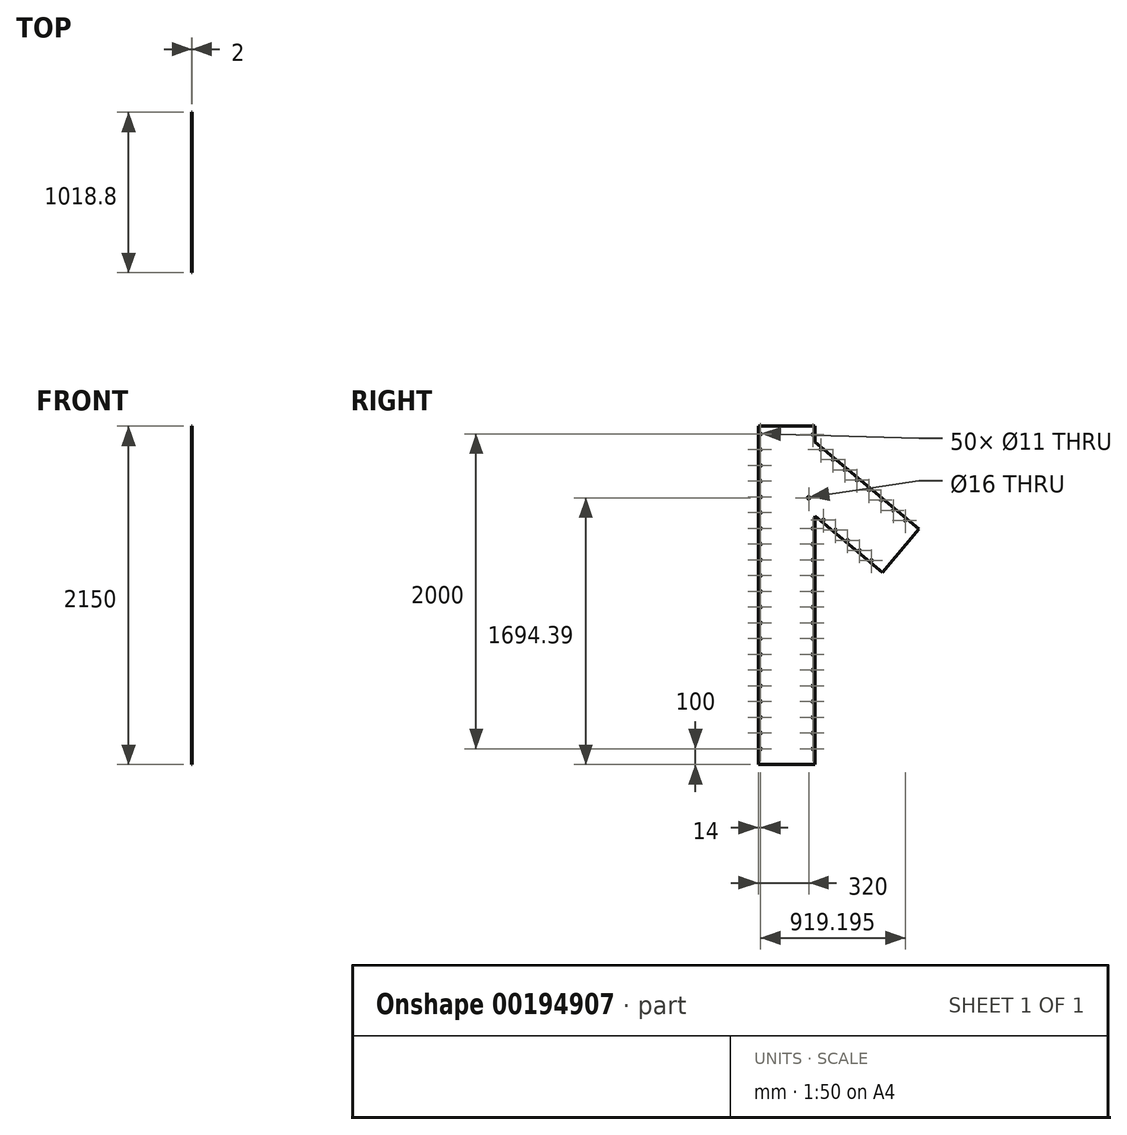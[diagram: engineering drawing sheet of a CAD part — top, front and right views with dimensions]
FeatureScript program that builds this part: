
annotation { "Feature Type Name" : "Feature", "Feature Type Description" : "" }
export const myFeature = defineFeature(function(context is Context, id is Id, definition is map)
    precondition{}
    {
        {
            var Q0;
            Q0=qCreatedBy(makeId("Right.planeOp"),FACE);
            var sketch = newSketch(context, id + "F0", { "sketchPlane" : qUnion([Q0])});
            skLineSegment(sketch, "E0", {"start": v(0, 0) * mm, "end": v(0, 2050) * mm});
            skLineSegment(sketch, "E1", {"start": v(360, 2050) * mm, "end": v(1018.8, 1497.2) * mm});
            skLineSegment(sketch, "E2", {"start": v(1018.8, 1497.2) * mm, "end": v(787.4, 1221.43) * mm});
            skLineSegment(sketch, "E3", {"start": v(360, 1580.05) * mm, "end": v(360, 0) * mm});
            skLineSegment(sketch, "E4", {"start": v(360, 0) * mm, "end": v(0, 0) * mm});
            skLineSegment(sketch, "E5", {"start": v(360, 2050) * mm, "end": v(360, 2150) * mm});
            skLineSegment(sketch, "E6", {"start": v(360, 2150) * mm, "end": v(0, 2150) * mm});
            skLineSegment(sketch, "E7", {"start": v(0, 2150) * mm, "end": v(0, 2050) * mm});
            skLineSegment(sketch, "E8", {"start": v(787.4, 1221.43) * mm, "end": v(360, 1580.05) * mm});
            skSolve(sketch);
        }
        {
            var Q0;
            Q0 = qSketchRegion(id + "F0", true);
            extrude(context, id + "F1", {"entities" : qUnion([Q0]), "depth" : 2 * mm});
        }
        {
            var Q0;
            Q0=makeQuery(id+"F1.opExtrude","CAP_FACE",FACE,{"disambiguationData":[OSD([sQuery(id+"F0.wireOp",EDGE,"E0"),sQuery(id+"F0.wireOp",EDGE,"E1"),sQuery(id+"F0.wireOp",EDGE,"E2"),sQuery(id+"F0.wireOp",EDGE,"E3"),sQuery(id+"F0.wireOp",EDGE,"E4"),sQuery(id+"F0.wireOp",EDGE,"E5"),sQuery(id+"F0.wireOp",EDGE,"E6"),sQuery(id+"F0.wireOp",EDGE,"E7"),sQuery(id+"F0.wireOp",EDGE,"E8")])],"isStart":false});
            var sketch = newSketch(context, id + "F2", { "sketchPlane" : qUnion([Q0])});
            skCircle(sketch, "E9", {"center": v(320, 1694.39) * mm, "radius": 8 * mm});
            skLineSegment(sketch, "E10", {"start": v(806.68, 1244.4) * mm, "end": v(330, 1644.39) * mm, "construction": true});
            skLineSegment(sketch, "E11", {"start": v(330, 1644.39) * mm, "end": v(330, 0) * mm, "construction": true});
            skLineSegment(sketch, "E12", {"start": v(14, 0) * mm, "end": v(14, 2150) * mm, "construction": true});
            skLineSegment(sketch, "E13", {"start": v(346, 2150) * mm, "end": v(346, 2043.47) * mm, "construction": true});
            skLineSegment(sketch, "E14", {"start": v(346, 2043.47) * mm, "end": v(1009.8, 1486.48) * mm, "construction": true});
            skLineSegment(sketch, "E15", {"start": v(796.4, 1232.15) * mm, "end": v(346, 1610.08) * mm, "construction": true});
            skLineSegment(sketch, "E16", {"start": v(346, 1610.08) * mm, "end": v(346, 0) * mm, "construction": true});
            skCircle(sketch, "E17", {"center": v(14, 100) * mm, "radius": 5.5 * mm});
            skCircle(sketch, "E18", {"center": v(346, 100) * mm, "radius": 5.5 * mm});
            skCircle(sketch, "E19", {"center": v(719.79, 1296.43) * mm, "radius": 5.5 * mm});
            skCircle(sketch, "E20", {"center": v(933.2, 1550.76) * mm, "radius": 5.5 * mm});
            skCircle(sketch, "E21", {"center": v(346, 2096.74) * mm, "radius": 5.5 * mm});
            skCircle(sketch, "E22", {"center": v(14, 200) * mm, "radius": 5.5 * mm});
            skCircle(sketch, "E23", {"center": v(14, 300) * mm, "radius": 5.5 * mm});
            skCircle(sketch, "E24", {"center": v(14, 400) * mm, "radius": 5.5 * mm});
            skCircle(sketch, "E25", {"center": v(14, 500) * mm, "radius": 5.5 * mm});
            skCircle(sketch, "E26", {"center": v(14, 600) * mm, "radius": 5.5 * mm});
            skCircle(sketch, "E27", {"center": v(14, 700) * mm, "radius": 5.5 * mm});
            skCircle(sketch, "E28", {"center": v(14, 800) * mm, "radius": 5.5 * mm});
            skCircle(sketch, "E29", {"center": v(14, 900) * mm, "radius": 5.5 * mm});
            skCircle(sketch, "E30", {"center": v(14, 1000) * mm, "radius": 5.5 * mm});
            skCircle(sketch, "E31", {"center": v(14, 1100) * mm, "radius": 5.5 * mm});
            skCircle(sketch, "E32", {"center": v(14, 1200) * mm, "radius": 5.5 * mm});
            skCircle(sketch, "E33", {"center": v(14, 1300) * mm, "radius": 5.5 * mm});
            skCircle(sketch, "E34", {"center": v(14, 1400) * mm, "radius": 5.5 * mm});
            skCircle(sketch, "E35", {"center": v(14, 1500) * mm, "radius": 5.5 * mm});
            skCircle(sketch, "E36", {"center": v(14, 1600) * mm, "radius": 5.5 * mm});
            skCircle(sketch, "E37", {"center": v(14, 1700) * mm, "radius": 5.5 * mm});
            skCircle(sketch, "E38", {"center": v(14, 1800) * mm, "radius": 5.5 * mm});
            skCircle(sketch, "E39", {"center": v(14, 1900) * mm, "radius": 5.5 * mm});
            skCircle(sketch, "E40", {"center": v(14, 2000) * mm, "radius": 5.5 * mm});
            skCircle(sketch, "E41", {"center": v(14, 2100) * mm, "radius": 5.5 * mm});
            skCircle(sketch, "E42", {"center": v(346, 200) * mm, "radius": 5.5 * mm});
            skCircle(sketch, "E43", {"center": v(346, 300) * mm, "radius": 5.5 * mm});
            skCircle(sketch, "E44", {"center": v(346, 400) * mm, "radius": 5.5 * mm});
            skCircle(sketch, "E45", {"center": v(346, 500) * mm, "radius": 5.5 * mm});
            skCircle(sketch, "E46", {"center": v(346, 600) * mm, "radius": 5.5 * mm});
            skCircle(sketch, "E47", {"center": v(346, 700) * mm, "radius": 5.5 * mm});
            skCircle(sketch, "E48", {"center": v(346, 800) * mm, "radius": 5.5 * mm});
            skCircle(sketch, "E49", {"center": v(346, 900) * mm, "radius": 5.5 * mm});
            skCircle(sketch, "E50", {"center": v(346, 1000) * mm, "radius": 5.5 * mm});
            skCircle(sketch, "E51", {"center": v(346, 1100) * mm, "radius": 5.5 * mm});
            skCircle(sketch, "E52", {"center": v(346, 1200) * mm, "radius": 5.5 * mm});
            skCircle(sketch, "E53", {"center": v(346, 1300) * mm, "radius": 5.5 * mm});
            skCircle(sketch, "E54", {"center": v(346, 1400) * mm, "radius": 5.5 * mm});
            skCircle(sketch, "E55", {"center": v(346, 1500) * mm, "radius": 5.5 * mm});
            skCircle(sketch, "E56", {"center": v(643.18, 1360.7) * mm, "radius": 5.5 * mm});
            skCircle(sketch, "E57", {"center": v(566.58, 1424.99) * mm, "radius": 5.5 * mm});
            skCircle(sketch, "E58", {"center": v(489.98, 1489.27) * mm, "radius": 5.5 * mm});
            skCircle(sketch, "E59", {"center": v(413.37, 1553.55) * mm, "radius": 5.5 * mm});
            skCircle(sketch, "E60", {"center": v(856.6, 1615.04) * mm, "radius": 5.5 * mm});
            skCircle(sketch, "E61", {"center": v(779.99, 1679.31) * mm, "radius": 5.5 * mm});
            skCircle(sketch, "E62", {"center": v(703.38, 1743.6) * mm, "radius": 5.5 * mm});
            skCircle(sketch, "E63", {"center": v(626.78, 1807.87) * mm, "radius": 5.5 * mm});
            skCircle(sketch, "E64", {"center": v(550.17, 1872.15) * mm, "radius": 5.5 * mm});
            skCircle(sketch, "E65", {"center": v(473.57, 1936.43) * mm, "radius": 5.5 * mm});
            skCircle(sketch, "E66", {"center": v(396.96, 2000.7) * mm, "radius": 5.5 * mm});
            skLineSegment(sketch, "E67", {"start": v(330, 2150) * mm, "end": v(330, 2036.01) * mm, "construction": true});
            skLineSegment(sketch, "E68", {"start": v(330, 2036.01) * mm, "end": v(999.51, 1474.22) * mm, "construction": true});
            skSolve(sketch);
        }
        {
            var Q0;
            Q0 = qSketchRegion(id + "F2", true);
            extrude(context, id + "F3", {"entities" : qUnion([Q0]), "operationType" : NewBodyOperationType.REMOVE, "oppositeDirection" : true, "depth" : 25 * mm});
        }
    });
